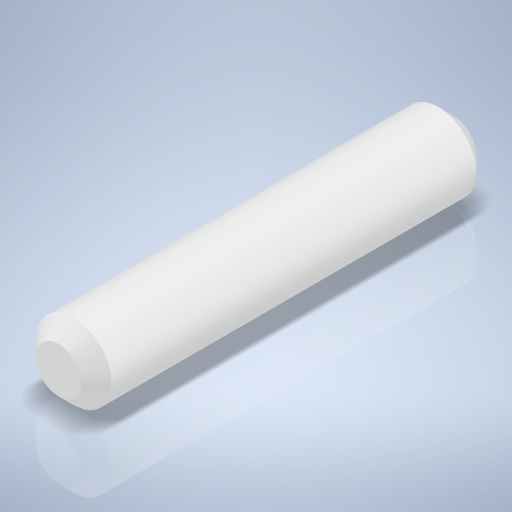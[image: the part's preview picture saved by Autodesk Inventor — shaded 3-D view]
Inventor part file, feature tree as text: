
AUTODESK INVENTOR PART (.ipt)
format: ipt  version: 2024 (Build 280153000, 153)  size: 243,712 bytes
history: native  units: mm
features: extrude x1, chamfer x1, sketch x1
ambient origin geometry x8: Origin, YZ Plane, XZ Plane, XY Plane, X Axis, Y Axis, Z Axis, Center Point
bodies: Volumenkörper1 (feature_tree)
feature tree (3):
  extrude  "Extrusion1"  Depth=13.0mm TaperAngle=0.0deg
  chamfer  "Fasen1"  Distance=0.5mm Angle=45.0deg
  sketch  "Skizze1"  dims[d0=2.5mm d1=13.0mm d2=0.0mm d3=0.5mm d4=2.0mm d5=45.0deg]
